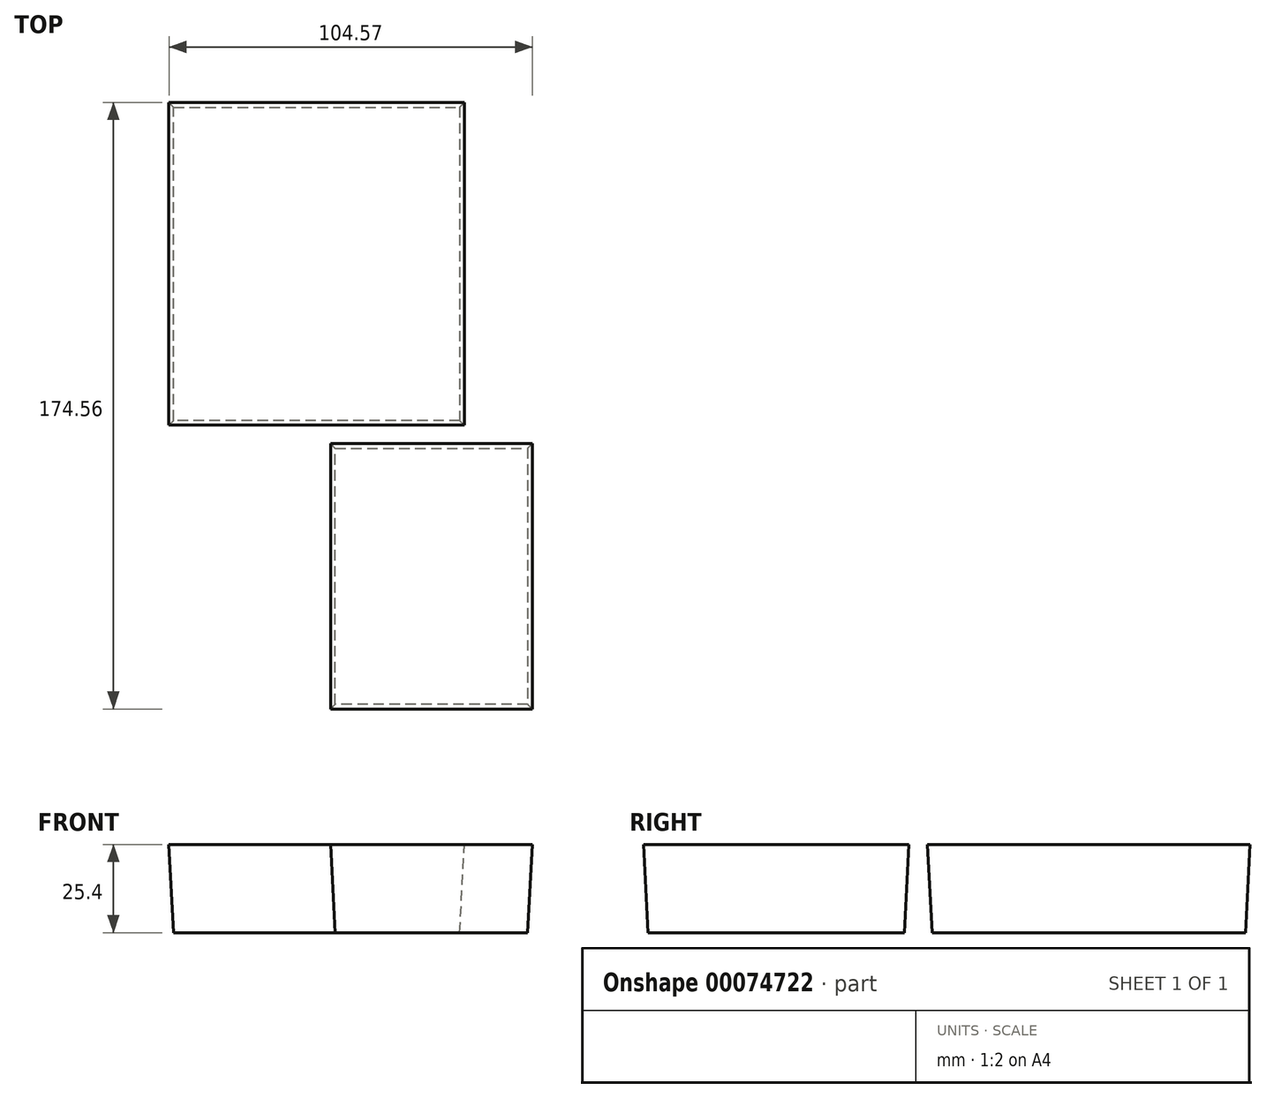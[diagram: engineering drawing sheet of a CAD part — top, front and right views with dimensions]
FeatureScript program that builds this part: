
annotation { "Feature Type Name" : "Feature", "Feature Type Description" : "" }
export const myFeature = defineFeature(function(context is Context, id is Id, definition is map)
    precondition{}
    {
        {
            var Q0;
            Q0=qCreatedBy(makeId("Top.planeOp"),FACE);
            var sketch = newSketch(context, id + "F1", { "sketchPlane" : qUnion([Q0])});
            skLineSegment(sketch, "E0.bottom", {"start": v(35.83, 46.9) * mm, "end": v(-46.51, 46.9) * mm});
            skLineSegment(sketch, "E0.top", {"start": v(35.83, -43.3) * mm, "end": v(-46.51, -43.3) * mm});
            skLineSegment(sketch, "E0.left", {"start": v(35.83, 46.9) * mm, "end": v(35.83, -43.3) * mm});
            skLineSegment(sketch, "E0.right", {"start": v(-46.51, 46.9) * mm, "end": v(-46.51, -43.3) * mm});
            skLineSegment(sketch, "E1.bottom", {"start": v(55.4, -51.32) * mm, "end": v(0, -51.32) * mm});
            skLineSegment(sketch, "E1.top", {"start": v(55.4, -125) * mm, "end": v(0, -125) * mm});
            skLineSegment(sketch, "E1.left", {"start": v(55.4, -51.32) * mm, "end": v(55.4, -125) * mm});
            skLineSegment(sketch, "E1.right", {"start": v(0, -51.32) * mm, "end": v(0, -125) * mm});
            skSolve(sketch);
        }
        {
            var Q0;
            Q0 = qSketchRegion(id + "F1", true);
            extrude(context, id + "F0", {"entities" : qUnion([Q0]), "depth" : 25.4 * mm, "hasDraft" : true, "draftAngle" : 3 * degree});
        }
    });
